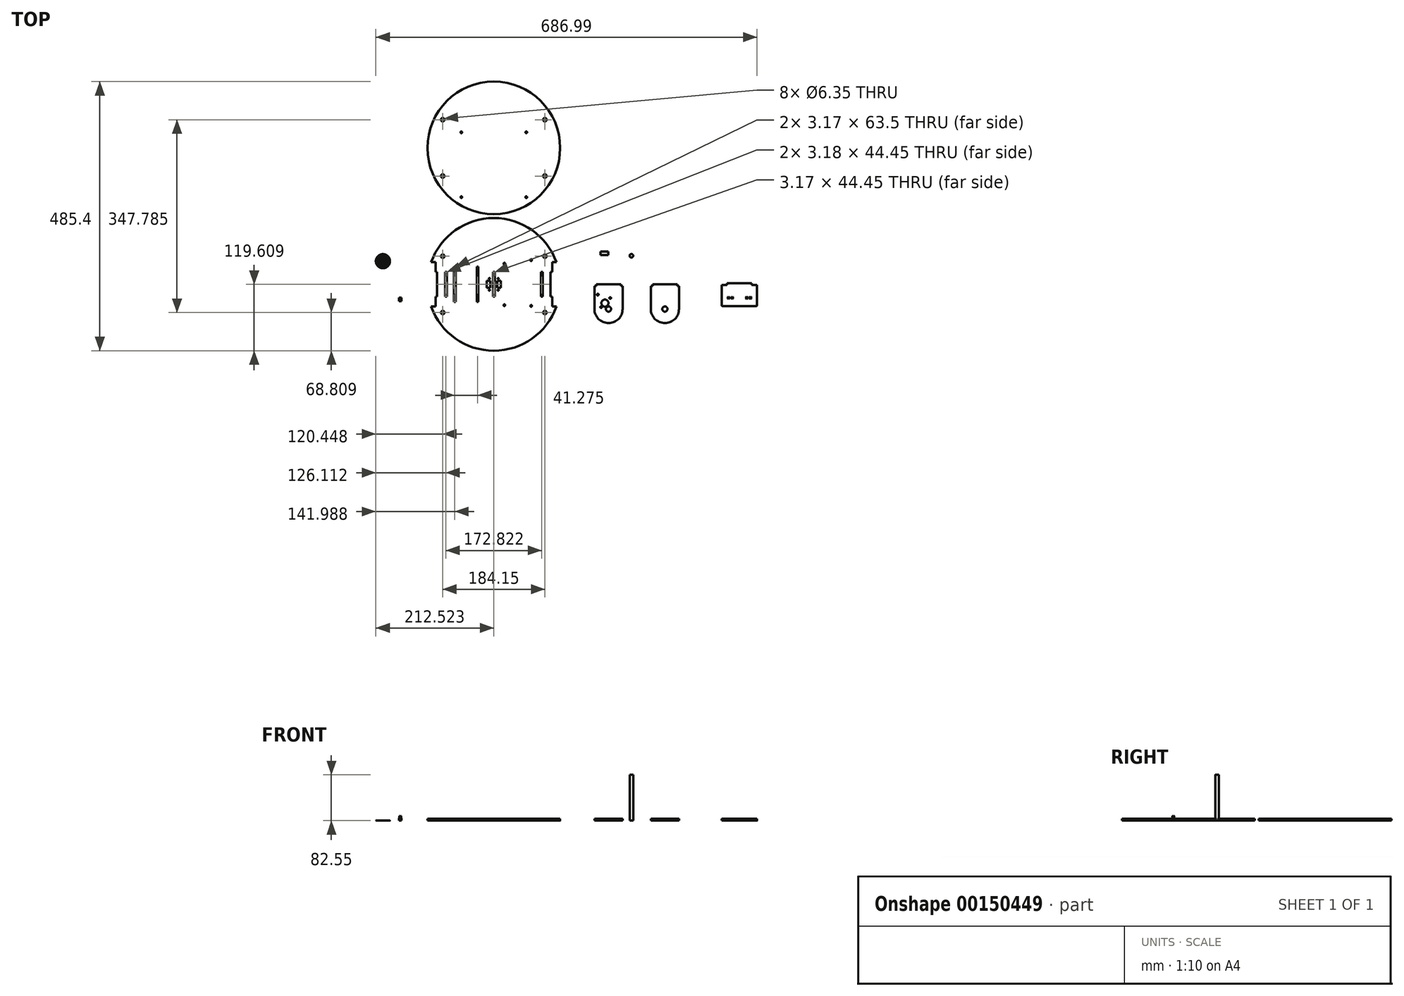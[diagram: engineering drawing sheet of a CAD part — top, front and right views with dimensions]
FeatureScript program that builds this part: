
annotation { "Feature Type Name" : "Feature", "Feature Type Description" : "" }
export const myFeature = defineFeature(function(context is Context, id is Id, definition is map)
    precondition{}
    {
        {
            var Q0;
            Q0=qCreatedBy(makeId("Top.planeOp"),FACE);
            var sketch = newSketch(context, id + "F0", { "sketchPlane" : qUnion([Q0])});
            skLineSegment(sketch, "E0", {"start": v(-7.62, 79.76) * mm, "end": v(0, 79.76) * mm});
            skLineSegment(sketch, "E1", {"start": v(0, 79.76) * mm, "end": v(0, 62.1) * mm});
            skLineSegment(sketch, "E2", {"start": v(0, 0) * mm, "end": v(-7.62, 0) * mm});
            skLineSegment(sketch, "E3", {"start": v(217.9, 79.76) * mm, "end": v(210.29, 79.76) * mm});
            skLineSegment(sketch, "E4", {"start": v(210.29, 79.76) * mm, "end": v(210.29, 62.1) * mm});
            skLineSegment(sketch, "E5", {"start": v(210.29, 0) * mm, "end": v(217.9, 0) * mm});
            skArc(sketch, "E6", {"start": v(217.9, 79.76) * mm, "mid": v(105.14, 159.49) * mm, "end": v(-7.62, 79.76) * mm});
            skArc(sketch, "E7", {"start": v(-7.62, 0) * mm, "mid": v(105.14, -79.73) * mm, "end": v(217.9, 0) * mm});
            skLineSegment(sketch, "E8", {"start": v(0, 39.88) * mm, "end": v(210.29, 39.88) * mm, "construction": true});
            skLineSegment(sketch, "E9", {"start": v(286.49, -4.57) * mm, "end": v(286.49, 36.7) * mm});
            skLineSegment(sketch, "E10", {"start": v(286.49, 36.7) * mm, "end": v(289.66, 36.7) * mm});
            skLineSegment(sketch, "E11", {"start": v(289.66, 36.7) * mm, "end": v(289.66, 39.88) * mm});
            skLineSegment(sketch, "E12", {"start": v(289.66, 39.88) * mm, "end": v(334.11, 39.88) * mm});
            skLineSegment(sketch, "E13", {"start": v(334.11, 39.88) * mm, "end": v(334.11, 36.7) * mm});
            skLineSegment(sketch, "E14", {"start": v(334.11, 36.7) * mm, "end": v(337.29, 36.7) * mm});
            skLineSegment(sketch, "E15", {"start": v(337.29, 36.7) * mm, "end": v(337.29, -4.57) * mm});
            skArc(sketch, "E16", {"start": v(286.49, -4.57) * mm, "mid": v(311.89, -29.97) * mm, "end": v(337.29, -4.57) * mm});
            skLineSegment(sketch, "E17", {"start": v(311.89, 39.88) * mm, "end": v(311.89, -31.9) * mm, "construction": true});
            skCircle(sketch, "E18", {"center": v(298.59, -1.03) * mm, "radius": 1.49 * mm});
            skCircle(sketch, "E19", {"center": v(314.99, 15.37) * mm, "radius": 1.49 * mm});
            skCircle(sketch, "E20", {"center": v(292.59, 21.37) * mm, "radius": 1.49 * mm});
            skCircle(sketch, "E21", {"center": v(305.43, 6.1) * mm, "radius": 6.41 * mm});
            skCircle(sketch, "E22", {"center": v(311.89, -4.57) * mm, "radius": 4.7 * mm});
            skLineSegment(sketch, "E23", {"start": v(292.59, 21.37) * mm, "end": v(298.59, -1.03) * mm, "construction": true});
            skLineSegment(sketch, "E24", {"start": v(298.59, -1.03) * mm, "end": v(314.99, 15.37) * mm, "construction": true});
            skLineSegment(sketch, "E25", {"start": v(314.99, 15.37) * mm, "end": v(292.59, 21.37) * mm, "construction": true});
            skLineSegment(sketch, "E26", {"start": v(305.43, 6.1) * mm, "end": v(321.71, 22.38) * mm, "construction": true});
            skLineSegment(sketch, "E27", {"start": v(210.29, 62.1) * mm, "end": v(207.11, 62.1) * mm});
            skLineSegment(sketch, "E28", {"start": v(207.11, 62.1) * mm, "end": v(207.11, 17.65) * mm});
            skLineSegment(sketch, "E29", {"start": v(207.11, 17.65) * mm, "end": v(210.29, 17.65) * mm});
            skLineSegment(sketch, "E30.trimOffspring", {"start": v(210.29, 17.65) * mm, "end": v(210.29, 0) * mm});
            skLineSegment(sketch, "E31", {"start": v(0, 62.1) * mm, "end": v(3.18, 62.1) * mm});
            skLineSegment(sketch, "E32", {"start": v(3.18, 62.1) * mm, "end": v(3.18, 17.65) * mm});
            skLineSegment(sketch, "E33", {"start": v(3.18, 17.65) * mm, "end": v(0, 17.65) * mm});
            skLineSegment(sketch, "E34.trimOffspring", {"start": v(0, 17.65) * mm, "end": v(0, 0) * mm});
            skLineSegment(sketch, "E35", {"start": v(388.09, -4.57) * mm, "end": v(388.09, 36.7) * mm});
            skLineSegment(sketch, "E36", {"start": v(388.09, 36.7) * mm, "end": v(391.26, 36.7) * mm});
            skLineSegment(sketch, "E37", {"start": v(391.26, 36.7) * mm, "end": v(391.26, 39.88) * mm});
            skLineSegment(sketch, "E38", {"start": v(391.26, 39.88) * mm, "end": v(435.71, 39.88) * mm});
            skLineSegment(sketch, "E39", {"start": v(435.71, 39.88) * mm, "end": v(435.71, 36.7) * mm});
            skLineSegment(sketch, "E40", {"start": v(435.71, 36.7) * mm, "end": v(438.89, 36.7) * mm});
            skLineSegment(sketch, "E41", {"start": v(438.89, 36.7) * mm, "end": v(438.89, -4.57) * mm});
            skArc(sketch, "E42", {"start": v(388.09, -4.57) * mm, "mid": v(413.49, -29.97) * mm, "end": v(438.89, -4.57) * mm});
            skLineSegment(sketch, "E43", {"start": v(413.49, 39.88) * mm, "end": v(413.49, -58.81) * mm, "construction": true});
            skCircle(sketch, "E44", {"center": v(413.49, -4.57) * mm, "radius": 4.7 * mm});
            skLineSegment(sketch, "E45.bottom", {"start": v(189.97, 62.1) * mm, "end": v(193.14, 62.1) * mm});
            skLineSegment(sketch, "E45.top", {"start": v(189.97, 17.65) * mm, "end": v(193.14, 17.65) * mm});
            skLineSegment(sketch, "E45.left", {"start": v(189.97, 62.1) * mm, "end": v(189.97, 17.65) * mm});
            skLineSegment(sketch, "E45.right", {"start": v(193.14, 62.1) * mm, "end": v(193.14, 17.65) * mm});
            skLineSegment(sketch, "E46.bottom", {"start": v(17.15, 62.1) * mm, "end": v(20.32, 62.1) * mm});
            skLineSegment(sketch, "E46.top", {"start": v(17.15, 17.65) * mm, "end": v(20.32, 17.65) * mm});
            skLineSegment(sketch, "E46.left", {"start": v(17.15, 62.1) * mm, "end": v(17.15, 17.65) * mm});
            skLineSegment(sketch, "E46.right", {"start": v(20.32, 62.1) * mm, "end": v(20.32, 17.65) * mm});
            skLineSegment(sketch, "E47", {"start": v(105.14, 39.88) * mm, "end": v(105.14, 78.68) * mm, "construction": true});
            skLineSegment(sketch, "E48.bottom", {"start": v(103.56, 62.1) * mm, "end": v(106.73, 62.1) * mm});
            skLineSegment(sketch, "E48.top", {"start": v(103.56, 17.65) * mm, "end": v(106.73, 17.65) * mm});
            skLineSegment(sketch, "E48.left", {"start": v(103.56, 62.1) * mm, "end": v(103.56, 17.65) * mm});
            skLineSegment(sketch, "E48.right", {"start": v(106.73, 62.1) * mm, "end": v(106.73, 17.65) * mm});
            skLineSegment(sketch, "E49", {"start": v(525.64, 41.8) * mm, "end": v(525.64, 38.62) * mm});
            skLineSegment(sketch, "E50", {"start": v(525.64, 38.62) * mm, "end": v(516.11, 38.62) * mm});
            skLineSegment(sketch, "E51", {"start": v(516.11, 38.62) * mm, "end": v(516.11, 2.1) * mm});
            skLineSegment(sketch, "E52", {"start": v(517.7, 0.52) * mm, "end": v(578.03, 0.52) * mm});
            skLineSegment(sketch, "E53", {"start": v(579.61, 2.1) * mm, "end": v(579.61, 38.62) * mm});
            skLineSegment(sketch, "E54", {"start": v(579.61, 38.62) * mm, "end": v(570.09, 38.62) * mm});
            skLineSegment(sketch, "E55", {"start": v(570.09, 38.62) * mm, "end": v(570.09, 41.8) * mm});
            skLineSegment(sketch, "E56", {"start": v(570.09, 41.8) * mm, "end": v(525.64, 41.8) * mm});
            skPoint(sketch, "E57.visualSharp", {"position": v(516.11, 0.52) * mm});
            skArc(sketch, "E57.filletArc", {"start": v(516.11, 2.1) * mm, "mid": v(516.58, 0.98) * mm, "end": v(517.7, 0.52) * mm});
            skPoint(sketch, "E58.visualSharp", {"position": v(579.61, 0.52) * mm});
            skArc(sketch, "E58.filletArc", {"start": v(578.03, 0.52) * mm, "mid": v(579.15, 0.98) * mm, "end": v(579.61, 2.1) * mm});
            skCircle(sketch, "E59", {"center": v(97.27, 50.3) * mm, "radius": 1.02 * mm});
            skCircle(sketch, "E60", {"center": v(113.02, 50.3) * mm, "radius": 1.02 * mm});
            skCircle(sketch, "E61", {"center": v(113.02, 29.47) * mm, "radius": 1.02 * mm});
            skCircle(sketch, "E62", {"center": v(97.27, 29.47) * mm, "radius": 1.02 * mm});
            skLineSegment(sketch, "E63.bottom", {"start": v(92.44, 46.23) * mm, "end": v(98.8, 46.23) * mm});
            skLineSegment(sketch, "E63.top", {"start": v(92.44, 33.53) * mm, "end": v(98.8, 33.53) * mm});
            skLineSegment(sketch, "E63.left", {"start": v(92.44, 46.23) * mm, "end": v(92.44, 33.53) * mm});
            skLineSegment(sketch, "E63.right", {"start": v(98.8, 46.23) * mm, "end": v(98.8, 33.53) * mm});
            skLineSegment(sketch, "E64.bottom", {"start": v(111.5, 46.23) * mm, "end": v(117.84, 46.23) * mm});
            skLineSegment(sketch, "E64.top", {"start": v(111.5, 33.53) * mm, "end": v(117.84, 33.53) * mm});
            skLineSegment(sketch, "E64.left", {"start": v(111.5, 46.23) * mm, "end": v(111.5, 33.53) * mm});
            skLineSegment(sketch, "E64.right", {"start": v(117.84, 46.23) * mm, "end": v(117.84, 33.53) * mm});
            skCircle(sketch, "E65", {"center": v(105.14, 286.06) * mm, "radius": 119.6 * mm});
            skCircle(sketch, "E66", {"center": v(13.07, 90.68) * mm, "radius": 3.18 * mm});
            skCircle(sketch, "E67", {"center": v(197.22, 90.68) * mm, "radius": 3.18 * mm});
            skCircle(sketch, "E68", {"center": v(197.22, -10.92) * mm, "radius": 3.18 * mm});
            skCircle(sketch, "E69", {"center": v(13.07, -10.92) * mm, "radius": 3.18 * mm});
            skLineSegment(sketch, "E70", {"start": v(105.14, 325.46) * mm, "end": v(105.14, 286.06) * mm, "construction": true});
            skLineSegment(sketch, "E71", {"start": v(150.45, 286.06) * mm, "end": v(105.14, 286.06) * mm, "construction": true});
            skCircle(sketch, "E72", {"center": v(13.07, 336.86) * mm, "radius": 3.18 * mm});
            skCircle(sketch, "E73", {"center": v(13.07, 235.26) * mm, "radius": 3.18 * mm});
            skCircle(sketch, "E74", {"center": v(197.22, 336.86) * mm, "radius": 3.18 * mm});
            skCircle(sketch, "E75", {"center": v(197.22, 235.26) * mm, "radius": 3.18 * mm});
            skLineSegment(sketch, "E76.bottom", {"start": v(297.3, 92.91) * mm, "end": v(311.27, 92.91) * mm});
            skLineSegment(sketch, "E76.top", {"start": v(297.3, 99.26) * mm, "end": v(311.27, 99.26) * mm});
            skLineSegment(sketch, "E76.left", {"start": v(297.3, 92.91) * mm, "end": v(297.3, 99.26) * mm});
            skLineSegment(sketch, "E76.right", {"start": v(311.27, 92.91) * mm, "end": v(311.27, 99.26) * mm});
            skCircle(sketch, "E77", {"center": v(46.64, 314.16) * mm, "radius": 1.5 * mm});
            skCircle(sketch, "E78", {"center": v(163.64, 314.16) * mm, "radius": 1.5 * mm});
            skCircle(sketch, "E79", {"center": v(163.64, 197.16) * mm, "radius": 1.5 * mm});
            skCircle(sketch, "E80", {"center": v(46.64, 197.16) * mm, "radius": 1.5 * mm});
            skCircle(sketch, "E81", {"center": v(124.2, 77.34) * mm, "radius": 1.5 * mm});
            skCircle(sketch, "E82", {"center": v(172.45, 83.7) * mm, "radius": 1.5 * mm});
            skCircle(sketch, "E83", {"center": v(124.2, 2.41) * mm, "radius": 1.5 * mm});
            skLineSegment(sketch, "E84.bottom", {"start": v(33.02, 71.63) * mm, "end": v(36.2, 71.63) * mm});
            skLineSegment(sketch, "E84.top", {"start": v(33.02, 8.13) * mm, "end": v(36.2, 8.13) * mm});
            skLineSegment(sketch, "E84.left", {"start": v(33.02, 71.63) * mm, "end": v(33.02, 8.13) * mm});
            skLineSegment(sketch, "E84.right", {"start": v(36.2, 71.63) * mm, "end": v(36.2, 8.13) * mm});
            skLineSegment(sketch, "E85.bottom", {"start": v(74.3, 71.63) * mm, "end": v(77.47, 71.63) * mm});
            skLineSegment(sketch, "E85.top", {"start": v(74.3, 8.13) * mm, "end": v(77.47, 8.13) * mm});
            skLineSegment(sketch, "E85.left", {"start": v(74.3, 71.63) * mm, "end": v(74.3, 8.13) * mm});
            skLineSegment(sketch, "E85.right", {"start": v(77.47, 71.63) * mm, "end": v(77.47, 8.13) * mm});
            skCircle(sketch, "E86", {"center": v(172.45, 1.14) * mm, "radius": 1.5 * mm});
            skSolve(sketch);
        }
        {
            var Q0;
            Q0 = qSketchRegion(id + "F0", true);
            extrude(context, id + "F1", {"entities" : qUnion([Q0]), "depth" : 3.17 * mm});
        }
        {
            var Q0;
            Q0=qCreatedBy(makeId("Top.planeOp"),FACE);
            var sketch = newSketch(context, id + "F2", { "sketchPlane" : qUnion([Q0])});
            skLineSegment(sketch, "E87.bottom", {"start": v(-65.73, 15.66) * mm, "end": v(-61.34, 15.66) * mm});
            skLineSegment(sketch, "E87.top", {"start": v(-65.73, 9.56) * mm, "end": v(-61.34, 9.56) * mm});
            skLineSegment(sketch, "E87.left", {"start": v(-65.73, 15.66) * mm, "end": v(-65.73, 9.56) * mm});
            skLineSegment(sketch, "E87.right", {"start": v(-61.34, 15.66) * mm, "end": v(-61.34, 9.56) * mm});
            skSolve(sketch);
        }
        {
            var Q0;
            Q0=makeQuery(id+"F2.imprint","IMPRINT",FACE,{"disambiguationData":[TD([[makeQuery(id+"F2.imprint","IMPRINT",EDGE,{"derivedFrom":sQuery(id+"F2.wireOp",EDGE,"E87.bottom")}),-1.0]])]});
            extrude(context, id + "F3", {"entities" : qUnion([Q0]), "depth" : 4.65 * mm});
        }
        {
            var Q0;
            Q0=makeQuery(id+"F3.opExtrude","CAP_FACE",FACE,{"disambiguationData":[OSD([sQuery(id+"F2.wireOp",EDGE,"E87.bottom"),sQuery(id+"F2.wireOp",EDGE,"E87.top"),sQuery(id+"F2.wireOp",EDGE,"E87.left"),sQuery(id+"F2.wireOp",EDGE,"E87.right")])],"isStart":false});
            var sketch = newSketch(context, id + "F4", { "sketchPlane" : qUnion([Q0])});
            skCircle(sketch, "E88", {"center": v(-64.59, 13.88) * mm, "radius": 0.25 * mm});
            skCircle(sketch, "E89", {"center": v(-62.48, 13.88) * mm, "radius": 0.25 * mm});
            skCircle(sketch, "E90", {"center": v(-64.59, 11.34) * mm, "radius": 0.25 * mm});
            skCircle(sketch, "E91", {"center": v(-62.48, 11.34) * mm, "radius": 0.25 * mm});
            skLineSegment(sketch, "E92", {"start": v(-63.53, 17.51) * mm, "end": v(-63.53, 6.65) * mm, "construction": true});
            skLineSegment(sketch, "E93", {"start": v(-69.48, 12.61) * mm, "end": v(-57.97, 12.61) * mm, "construction": true});
            skSolve(sketch);
        }
        {
            var Q0;
            Q0 = qSketchRegion(id + "F4", true);
            extrude(context, id + "F5", {"entities" : qUnion([Q0]), "operationType" : NewBodyOperationType.ADD, "depth" : 3.8 * mm});
        }
        {
            var Q0;
            Q0=makeQuery(id+"F3.opExtrude","CAP_FACE",FACE,{"disambiguationData":[OSD([sQuery(id+"F2.wireOp",EDGE,"E87.bottom"),sQuery(id+"F2.wireOp",EDGE,"E87.top"),sQuery(id+"F2.wireOp",EDGE,"E87.left"),sQuery(id+"F2.wireOp",EDGE,"E87.right")])],"isStart":true});
            var sketch = newSketch(context, id + "F6", { "sketchPlane" : qUnion([Q0])});
            skLineSegment(sketch, "E94.bottom", {"start": v(-61.93, -14.26) * mm, "end": v(-62.94, -14.26) * mm});
            skLineSegment(sketch, "E94.top", {"start": v(-61.93, -10.96) * mm, "end": v(-62.94, -10.96) * mm});
            skLineSegment(sketch, "E94.left", {"start": v(-61.93, -14.26) * mm, "end": v(-61.93, -10.96) * mm});
            skLineSegment(sketch, "E94.right", {"start": v(-62.94, -14.26) * mm, "end": v(-62.94, -10.96) * mm});
            skLineSegment(sketch, "E95.bottom", {"start": v(-64.12, -14.26) * mm, "end": v(-65.14, -14.26) * mm});
            skLineSegment(sketch, "E95.top", {"start": v(-64.12, -10.96) * mm, "end": v(-65.14, -10.96) * mm});
            skLineSegment(sketch, "E95.left", {"start": v(-64.12, -14.26) * mm, "end": v(-64.12, -10.96) * mm});
            skLineSegment(sketch, "E95.right", {"start": v(-65.14, -14.26) * mm, "end": v(-65.14, -10.96) * mm});
            skLineSegment(sketch, "E96", {"start": v(-63.53, -17.24) * mm, "end": v(-63.53, -7.22) * mm, "construction": true});
            skLineSegment(sketch, "E97", {"start": v(-59.5, -12.61) * mm, "end": v(-67.76, -12.61) * mm, "construction": true});
            skSolve(sketch);
        }
        {
            var Q0;
            Q0 = qSketchRegion(id + "F6", true);
            extrude(context, id + "F7", {"entities" : qUnion([Q0]), "operationType" : NewBodyOperationType.REMOVE, "oppositeDirection" : true, "depth" : 0.25 * mm});
        }
        {
            var Q0;
            Q0=makeQuery(id+"F1.opExtrude","CAP_FACE",FACE,{"disambiguationData":[OSD([sQuery(id+"F0.wireOp",EDGE,"E49"),sQuery(id+"F0.wireOp",EDGE,"E50"),sQuery(id+"F0.wireOp",EDGE,"E51"),sQuery(id+"F0.wireOp",EDGE,"E52"),sQuery(id+"F0.wireOp",EDGE,"E53"),sQuery(id+"F0.wireOp",EDGE,"E54"),sQuery(id+"F0.wireOp",EDGE,"E55"),sQuery(id+"F0.wireOp",EDGE,"E56"),sQuery(id+"F0.wireOp",EDGE,"E57.filletArc"),sQuery(id+"F0.wireOp",EDGE,"E58.filletArc")])],"isStart":true});
            var sketch = newSketch(context, id + "F8", { "sketchPlane" : qUnion([Q0])});
            skCircle(sketch, "E98", {"center": v(539.1, -15.55) * mm, "radius": 12.7 * mm, "construction": true});
            skCircle(sketch, "E99", {"center": v(556.63, -15.55) * mm, "radius": 12.7 * mm, "construction": true});
            skCircle(sketch, "E100", {"center": v(539.1, -15.55) * mm, "radius": 6.35 * mm, "construction": true});
            skCircle(sketch, "E101", {"center": v(556.63, -15.55) * mm, "radius": 6.35 * mm, "construction": true});
            skCircle(sketch, "E102", {"center": v(527.03, -16.6) * mm, "radius": 0.38 * mm});
            skCircle(sketch, "E103", {"center": v(529.57, -16.6) * mm, "radius": 0.38 * mm});
            skCircle(sketch, "E104", {"center": v(527.03, -14.5) * mm, "radius": 0.38 * mm});
            skCircle(sketch, "E105", {"center": v(529.57, -14.5) * mm, "radius": 0.38 * mm});
            skCircle(sketch, "E106", {"center": v(533.38, -16.6) * mm, "radius": 0.38 * mm});
            skCircle(sketch, "E107", {"center": v(535.92, -16.6) * mm, "radius": 0.38 * mm});
            skCircle(sketch, "E108", {"center": v(533.38, -14.5) * mm, "radius": 0.38 * mm});
            skCircle(sketch, "E109", {"center": v(535.92, -14.5) * mm, "radius": 0.38 * mm});
            skLineSegment(sketch, "E110", {"start": v(539.1, -15.55) * mm, "end": v(556.63, -15.55) * mm, "construction": true});
            skCircle(sketch, "E111", {"center": v(559.8, -16.6) * mm, "radius": 0.38 * mm});
            skCircle(sketch, "E112", {"center": v(562.34, -16.6) * mm, "radius": 0.38 * mm});
            skCircle(sketch, "E113", {"center": v(559.8, -14.5) * mm, "radius": 0.38 * mm});
            skCircle(sketch, "E114", {"center": v(562.34, -14.5) * mm, "radius": 0.38 * mm});
            skCircle(sketch, "E115", {"center": v(566.15, -16.6) * mm, "radius": 0.38 * mm});
            skCircle(sketch, "E116", {"center": v(568.7, -16.6) * mm, "radius": 0.38 * mm});
            skCircle(sketch, "E117", {"center": v(566.15, -14.5) * mm, "radius": 0.38 * mm});
            skCircle(sketch, "E118", {"center": v(568.7, -14.5) * mm, "radius": 0.38 * mm});
            skSolve(sketch);
        }
        {
            var Q0;
            Q0 = qSketchRegion(id + "F8", true);
            extrude(context, id + "F9", {"entities" : qUnion([Q0]), "operationType" : NewBodyOperationType.REMOVE, "endBound" : BoundingType.THROUGH_ALL, "oppositeDirection" : true, "depth" : 25.4 * mm});
        }
        {
            var Q0;
            Q0=qCreatedBy(makeId("Top.planeOp"),FACE);
            var sketch = newSketch(context, id + "F10", { "sketchPlane" : qUnion([Q0])});
            skCircle(sketch, "E119", {"center": v(-94.68, 81.7) * mm, "radius": 12.7 * mm});
            skSolve(sketch);
        }
        {
            var Q0;
            Q0 = qSketchRegion(id + "F10", true);
            extrude(context, id + "F11", {"entities" : qUnion([Q0]), "depth" : 0.25 * mm});
        }
        {
            var Q0;
            Q0=makeQuery(id+"F11.opExtrude","CAP_FACE",FACE,{"disambiguationData":[OSD([sQuery(id+"F10.wireOp",EDGE,"E119")])],"isStart":false});
            var sketch = newSketch(context, id + "F12", { "sketchPlane" : qUnion([Q0])});
            skLineSegment(sketch, "E120", {"start": v(-94.68, 88.06) * mm, "end": v(-94.68, 94.4) * mm});
            skLineSegment(sketch, "E121", {"start": v(-90.76, 93.78) * mm, "end": v(-92.72, 87.74) * mm});
            skArc(sketch, "E122", {"start": v(-94.68, 88.06) * mm, "mid": v(-94.18, 88.04) * mm, "end": v(-93.69, 87.98) * mm});
            skArc(sketch, "E123", {"start": v(-94.68, 94.4) * mm, "mid": v(-92.7, 94.25) * mm, "end": v(-90.76, 93.78) * mm});
            skArc(sketch, "E124", {"start": v(-92.72, 87.74) * mm, "mid": v(-92.25, 87.57) * mm, "end": v(-91.8, 87.36) * mm});
            skLineSegment(sketch, "E125", {"start": v(-94.64, 81.96) * mm, "end": v(-93.69, 87.98) * mm});
            skLineSegment(sketch, "E126", {"start": v(-94.57, 81.93) * mm, "end": v(-91.8, 87.36) * mm});
            skArc(sketch, "E127", {"start": v(-94.64, 81.96) * mm, "mid": v(-94.6, 81.95) * mm, "end": v(-94.57, 81.93) * mm});
            skLineSegment(sketch, "E128.1.0", {"start": v(-98.41, 86.84) * mm, "end": v(-102.15, 91.98) * mm});
            skArc(sketch, "E128.1.1", {"start": v(-102.15, 91.98) * mm, "mid": v(-100.45, 93.02) * mm, "end": v(-98.6, 93.78) * mm});
            skLineSegment(sketch, "E128.1.2", {"start": v(-98.6, 93.78) * mm, "end": v(-96.64, 87.74) * mm});
            skArc(sketch, "E128.1.3", {"start": v(-96.64, 87.74) * mm, "mid": v(-96.16, 87.88) * mm, "end": v(-95.67, 87.98) * mm});
            skLineSegment(sketch, "E128.1.4", {"start": v(-94.72, 81.96) * mm, "end": v(-95.67, 87.98) * mm});
            skArc(sketch, "E128.1.5", {"start": v(-98.41, 86.84) * mm, "mid": v(-98, 87.12) * mm, "end": v(-97.56, 87.36) * mm});
            skLineSegment(sketch, "E128.1.6", {"start": v(-94.8, 81.93) * mm, "end": v(-97.56, 87.36) * mm});
            skArc(sketch, "E128.1.7", {"start": v(-94.8, 81.93) * mm, "mid": v(-94.76, 81.95) * mm, "end": v(-94.72, 81.96) * mm});
            skLineSegment(sketch, "E128.2.0", {"start": v(-100.72, 83.67) * mm, "end": v(-106.76, 85.63) * mm});
            skArc(sketch, "E128.2.1", {"start": v(-106.76, 85.63) * mm, "mid": v(-106, 87.47) * mm, "end": v(-104.96, 89.17) * mm});
            skLineSegment(sketch, "E128.2.2", {"start": v(-104.96, 89.17) * mm, "end": v(-99.82, 85.44) * mm});
            skArc(sketch, "E128.2.3", {"start": v(-99.82, 85.44) * mm, "mid": v(-99.5, 85.83) * mm, "end": v(-99.17, 86.2) * mm});
            skLineSegment(sketch, "E128.2.4", {"start": v(-94.86, 81.89) * mm, "end": v(-99.17, 86.2) * mm});
            skArc(sketch, "E128.2.5", {"start": v(-100.72, 83.67) * mm, "mid": v(-100.55, 84.14) * mm, "end": v(-100.34, 84.59) * mm});
            skLineSegment(sketch, "E128.2.6", {"start": v(-94.9, 81.82) * mm, "end": v(-100.34, 84.59) * mm});
            skArc(sketch, "E128.2.7", {"start": v(-94.9, 81.82) * mm, "mid": v(-94.89, 81.85) * mm, "end": v(-94.86, 81.89) * mm});
            skLineSegment(sketch, "E129.1.3.0", {"start": v(-100.72, 79.74) * mm, "end": v(-106.76, 77.78) * mm});
            skArc(sketch, "E129.3.3.0", {"start": v(-106.76, 77.78) * mm, "mid": v(-107.22, 79.72) * mm, "end": v(-107.38, 81.7) * mm});
            skLineSegment(sketch, "E129.7.3.0", {"start": v(-107.38, 81.7) * mm, "end": v(-101.03, 81.7) * mm});
            skArc(sketch, "E129.10.3.0", {"start": v(-101.03, 81.7) * mm, "mid": v(-101.01, 82.2) * mm, "end": v(-100.95, 82.7) * mm});
            skLineSegment(sketch, "E129.14.3.0", {"start": v(-94.93, 81.75) * mm, "end": v(-100.95, 82.7) * mm});
            skArc(sketch, "E129.17.3.0", {"start": v(-100.72, 79.74) * mm, "mid": v(-100.86, 80.22) * mm, "end": v(-100.95, 80.71) * mm});
            skLineSegment(sketch, "E129.21.3.0", {"start": v(-94.93, 81.67) * mm, "end": v(-100.95, 80.71) * mm});
            skArc(sketch, "E129.24.3.0", {"start": v(-94.93, 81.67) * mm, "mid": v(-94.93, 81.7) * mm, "end": v(-94.93, 81.75) * mm});
            skLineSegment(sketch, "E129.1.4.0", {"start": v(-98.41, 76.57) * mm, "end": v(-102.15, 71.43) * mm});
            skArc(sketch, "E129.3.4.0", {"start": v(-102.15, 71.43) * mm, "mid": v(-103.66, 72.73) * mm, "end": v(-104.96, 74.24) * mm});
            skLineSegment(sketch, "E129.7.4.0", {"start": v(-104.96, 74.24) * mm, "end": v(-99.82, 77.97) * mm});
            skArc(sketch, "E129.10.4.0", {"start": v(-99.82, 77.97) * mm, "mid": v(-100.1, 78.39) * mm, "end": v(-100.34, 78.82) * mm});
            skLineSegment(sketch, "E129.14.4.0", {"start": v(-94.9, 81.6) * mm, "end": v(-100.34, 78.82) * mm});
            skArc(sketch, "E129.17.4.0", {"start": v(-98.41, 76.57) * mm, "mid": v(-98.8, 76.88) * mm, "end": v(-99.17, 77.22) * mm});
            skLineSegment(sketch, "E129.21.4.0", {"start": v(-94.86, 81.53) * mm, "end": v(-99.17, 77.22) * mm});
            skArc(sketch, "E129.24.4.0", {"start": v(-94.86, 81.53) * mm, "mid": v(-94.89, 81.56) * mm, "end": v(-94.9, 81.6) * mm});
            skLineSegment(sketch, "E129.1.5.0", {"start": v(-94.68, 75.36) * mm, "end": v(-94.68, 69) * mm});
            skArc(sketch, "E129.3.5.0", {"start": v(-94.68, 69) * mm, "mid": v(-96.67, 69.16) * mm, "end": v(-98.6, 69.63) * mm});
            skLineSegment(sketch, "E129.7.5.0", {"start": v(-98.6, 69.63) * mm, "end": v(-96.64, 75.67) * mm});
            skArc(sketch, "E129.10.5.0", {"start": v(-96.64, 75.67) * mm, "mid": v(-97.11, 75.84) * mm, "end": v(-97.56, 76.05) * mm});
            skLineSegment(sketch, "E129.14.5.0", {"start": v(-94.8, 81.48) * mm, "end": v(-97.56, 76.05) * mm});
            skArc(sketch, "E129.17.5.0", {"start": v(-94.68, 75.36) * mm, "mid": v(-95.18, 75.37) * mm, "end": v(-95.67, 75.43) * mm});
            skLineSegment(sketch, "E129.21.5.0", {"start": v(-94.72, 81.45) * mm, "end": v(-95.67, 75.43) * mm});
            skArc(sketch, "E129.24.5.0", {"start": v(-94.72, 81.45) * mm, "mid": v(-94.76, 81.46) * mm, "end": v(-94.8, 81.48) * mm});
            skLineSegment(sketch, "E129.1.6.0", {"start": v(-90.95, 76.57) * mm, "end": v(-87.22, 71.43) * mm});
            skArc(sketch, "E129.3.6.0", {"start": v(-87.22, 71.43) * mm, "mid": v(-88.91, 70.39) * mm, "end": v(-90.76, 69.63) * mm});
            skLineSegment(sketch, "E129.7.6.0", {"start": v(-90.76, 69.63) * mm, "end": v(-92.72, 75.67) * mm});
            skArc(sketch, "E129.10.6.0", {"start": v(-92.72, 75.67) * mm, "mid": v(-93.2, 75.53) * mm, "end": v(-93.69, 75.43) * mm});
            skLineSegment(sketch, "E129.14.6.0", {"start": v(-94.64, 81.45) * mm, "end": v(-93.69, 75.43) * mm});
            skArc(sketch, "E129.17.6.0", {"start": v(-90.95, 76.57) * mm, "mid": v(-91.36, 76.3) * mm, "end": v(-91.8, 76.05) * mm});
            skLineSegment(sketch, "E129.21.6.0", {"start": v(-94.57, 81.48) * mm, "end": v(-91.8, 76.05) * mm});
            skArc(sketch, "E129.24.6.0", {"start": v(-94.57, 81.48) * mm, "mid": v(-94.6, 81.46) * mm, "end": v(-94.64, 81.45) * mm});
            skLineSegment(sketch, "E129.1.7.0", {"start": v(-88.64, 79.74) * mm, "end": v(-82.6, 77.78) * mm});
            skArc(sketch, "E129.3.7.0", {"start": v(-82.6, 77.78) * mm, "mid": v(-83.36, 75.94) * mm, "end": v(-84.4, 74.24) * mm});
            skLineSegment(sketch, "E129.7.7.0", {"start": v(-84.4, 74.24) * mm, "end": v(-89.54, 77.97) * mm});
            skArc(sketch, "E129.10.7.0", {"start": v(-89.54, 77.97) * mm, "mid": v(-89.85, 77.58) * mm, "end": v(-90.2, 77.22) * mm});
            skLineSegment(sketch, "E129.14.7.0", {"start": v(-94.5, 81.53) * mm, "end": v(-90.2, 77.22) * mm});
            skArc(sketch, "E129.17.7.0", {"start": v(-88.64, 79.74) * mm, "mid": v(-88.81, 79.28) * mm, "end": v(-89.02, 78.82) * mm});
            skLineSegment(sketch, "E129.21.7.0", {"start": v(-94.45, 81.6) * mm, "end": v(-89.02, 78.82) * mm});
            skArc(sketch, "E129.24.7.0", {"start": v(-94.45, 81.6) * mm, "mid": v(-94.48, 81.56) * mm, "end": v(-94.5, 81.53) * mm});
            skLineSegment(sketch, "E129.1.8.0", {"start": v(-88.64, 83.67) * mm, "end": v(-82.6, 85.63) * mm});
            skArc(sketch, "E129.3.8.0", {"start": v(-82.6, 85.63) * mm, "mid": v(-82.14, 83.7) * mm, "end": v(-81.98, 81.7) * mm});
            skLineSegment(sketch, "E129.7.8.0", {"start": v(-81.98, 81.7) * mm, "end": v(-88.33, 81.7) * mm});
            skArc(sketch, "E129.10.8.0", {"start": v(-88.33, 81.7) * mm, "mid": v(-88.35, 81.2) * mm, "end": v(-88.4, 80.71) * mm});
            skLineSegment(sketch, "E129.14.8.0", {"start": v(-94.43, 81.67) * mm, "end": v(-88.4, 80.71) * mm});
            skArc(sketch, "E129.17.8.0", {"start": v(-88.64, 83.67) * mm, "mid": v(-88.5, 83.19) * mm, "end": v(-88.4, 82.7) * mm});
            skLineSegment(sketch, "E129.21.8.0", {"start": v(-94.43, 81.75) * mm, "end": v(-88.4, 82.7) * mm});
            skArc(sketch, "E129.24.8.0", {"start": v(-94.43, 81.75) * mm, "mid": v(-94.43, 81.7) * mm, "end": v(-94.43, 81.67) * mm});
            skLineSegment(sketch, "E129.1.9.0", {"start": v(-90.95, 86.84) * mm, "end": v(-87.22, 91.98) * mm});
            skArc(sketch, "E129.3.9.0", {"start": v(-87.22, 91.98) * mm, "mid": v(-85.7, 90.69) * mm, "end": v(-84.4, 89.17) * mm});
            skLineSegment(sketch, "E129.7.9.0", {"start": v(-84.4, 89.17) * mm, "end": v(-89.54, 85.44) * mm});
            skArc(sketch, "E129.10.9.0", {"start": v(-89.54, 85.44) * mm, "mid": v(-89.27, 85.02) * mm, "end": v(-89.02, 84.59) * mm});
            skLineSegment(sketch, "E129.14.9.0", {"start": v(-94.45, 81.82) * mm, "end": v(-89.02, 84.59) * mm});
            skArc(sketch, "E129.17.9.0", {"start": v(-90.95, 86.84) * mm, "mid": v(-90.56, 86.53) * mm, "end": v(-90.2, 86.2) * mm});
            skLineSegment(sketch, "E129.21.9.0", {"start": v(-94.5, 81.89) * mm, "end": v(-90.2, 86.2) * mm});
            skArc(sketch, "E129.24.9.0", {"start": v(-94.5, 81.89) * mm, "mid": v(-94.48, 81.85) * mm, "end": v(-94.45, 81.82) * mm});
            skSolve(sketch);
        }
        {
            var Q0;
            Q0 = qSketchRegion(id + "F12", true);
            extrude(context, id + "F13", {"entities" : qUnion([Q0]), "operationType" : NewBodyOperationType.REMOVE, "oppositeDirection" : true, "depth" : 0.05 * mm});
        }
        {
            var Q0;
            Q0=qCreatedBy(makeId("Top.planeOp"),FACE);
            var sketch = newSketch(context, id + "F14", { "sketchPlane" : qUnion([Q0])});
            skCircle(sketch, "E130", {"center": v(353.13, 91.5) * mm, "radius": 3.18 * mm});
            skSolve(sketch);
        }
        {
            var Q0;
            Q0=makeQuery(id+"F14.imprint","IMPRINT",FACE,{"disambiguationData":[TD([[makeQuery(id+"F14.imprint","IMPRINT",EDGE,{"derivedFrom":sQuery(id+"F14.wireOp",EDGE,"E130")}),1.0]])]});
            extrude(context, id + "F15", {"entities" : qUnion([Q0]), "depth" : 82.55 * mm});
        }
    });
